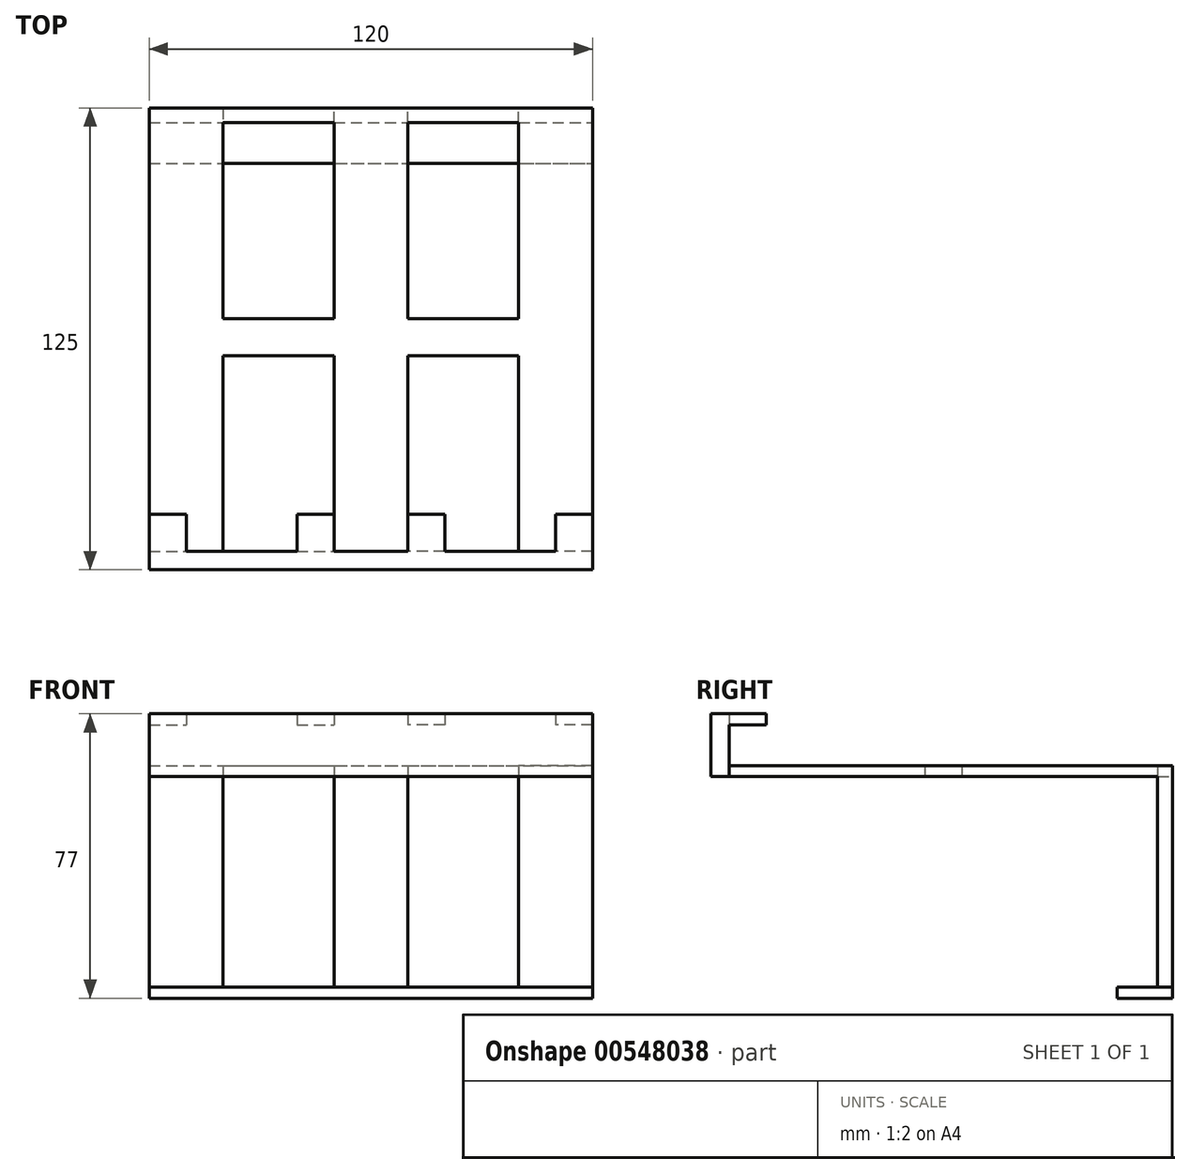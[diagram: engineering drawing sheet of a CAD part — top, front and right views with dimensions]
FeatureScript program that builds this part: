
annotation { "Feature Type Name" : "Feature", "Feature Type Description" : "" }
export const myFeature = defineFeature(function(context is Context, id is Id, definition is map)
    precondition{}
    {
        {
            var Q0;
            Q0=qCreatedBy(makeId("Top.planeOp"),FACE);
            var sketch = newSketch(context, id + "F0", { "sketchPlane" : qUnion([Q0])});
            skLineSegment(sketch, "E0.bottom", {"start": v(-56.42, -42.97) * mm, "end": v(63.58, -42.97) * mm});
            skLineSegment(sketch, "E0.top", {"start": v(-56.42, -47.97) * mm, "end": v(63.58, -47.97) * mm});
            skLineSegment(sketch, "E0.left", {"start": v(-56.42, -42.97) * mm, "end": v(-56.42, -47.97) * mm});
            skLineSegment(sketch, "E0.right", {"start": v(63.58, -42.97) * mm, "end": v(63.58, -47.97) * mm});
            skSolve(sketch);
        }
        {
            var Q0;
            Q0=makeQuery(id+"F0.imprint","IMPRINT",FACE,{"disambiguationData":[TD([[makeQuery(id+"F0.imprint","IMPRINT",EDGE,{"derivedFrom":sQuery(id+"F0.wireOp",EDGE,"E0.bottom")}),-1.0]])]});
            extrude(context, id + "F1", {"entities" : qUnion([Q0]), "depth" : 17 * mm, "offsetDistance" : 25 * mm});
        }
        {
            var Q0;
            Q0=makeQuery(id+"F1.opExtrude","SWEPT_FACE",FACE,{"disambiguationData":[OSD([sQuery(id+"F0.wireOp",EDGE,"E0.bottom")])]});
            var sketch = newSketch(context, id + "F2", { "sketchPlane" : qUnion([Q0])});
            skLineSegment(sketch, "E1.bottom", {"start": v(56.42, 17) * mm, "end": v(46.42, 17) * mm});
            skLineSegment(sketch, "E1.top", {"start": v(56.42, 14) * mm, "end": v(46.42, 14) * mm});
            skLineSegment(sketch, "E1.left", {"start": v(56.42, 17) * mm, "end": v(56.42, 14) * mm});
            skLineSegment(sketch, "E1.right", {"start": v(46.42, 17) * mm, "end": v(46.42, 14) * mm});
            skLineSegment(sketch, "E2.bottom", {"start": v(-63.58, 17) * mm, "end": v(-53.58, 17) * mm});
            skLineSegment(sketch, "E2.top", {"start": v(-63.58, 14) * mm, "end": v(-53.58, 14) * mm});
            skLineSegment(sketch, "E2.left", {"start": v(-63.58, 17) * mm, "end": v(-63.58, 14) * mm});
            skLineSegment(sketch, "E2.right", {"start": v(-53.58, 17) * mm, "end": v(-53.58, 14) * mm});
            skLineSegment(sketch, "E3.bottom", {"start": v(16.42, 17) * mm, "end": v(6.42, 17) * mm});
            skLineSegment(sketch, "E3.top", {"start": v(16.42, 14) * mm, "end": v(6.42, 14) * mm});
            skLineSegment(sketch, "E3.left", {"start": v(16.42, 17) * mm, "end": v(16.42, 14) * mm});
            skLineSegment(sketch, "E3.right", {"start": v(6.42, 17) * mm, "end": v(6.42, 14) * mm});
            skLineSegment(sketch, "E4.bottom", {"start": v(-23.58, 17) * mm, "end": v(-13.58, 17) * mm});
            skLineSegment(sketch, "E4.top", {"start": v(-23.58, 14) * mm, "end": v(-13.58, 14) * mm});
            skLineSegment(sketch, "E4.left", {"start": v(-23.58, 17) * mm, "end": v(-23.58, 14) * mm});
            skLineSegment(sketch, "E4.right", {"start": v(-13.58, 17) * mm, "end": v(-13.58, 14) * mm});
            skSolve(sketch);
        }
        {
            var Q0;
            Q0 = qSketchRegion(id + "F2", true);
            extrude(context, id + "F3", {"entities" : qUnion([Q0]), "operationType" : NewBodyOperationType.ADD, "depth" : 10 * mm, "offsetDistance" : 25 * mm});
        }
        {
            var Q0;
            Q0=makeQuery(id+"F1.opExtrude","SWEPT_FACE",FACE,{"disambiguationData":[OSD([sQuery(id+"F0.wireOp",EDGE,"E0.bottom")])]});
            var sketch = newSketch(context, id + "F4", { "sketchPlane" : qUnion([Q0])});
            skLineSegment(sketch, "E5.bottom", {"start": v(56.42, 0) * mm, "end": v(36.42, 0) * mm});
            skLineSegment(sketch, "E5.top", {"start": v(56.42, 3) * mm, "end": v(36.42, 3) * mm});
            skLineSegment(sketch, "E5.left", {"start": v(56.42, 0) * mm, "end": v(56.42, 3) * mm});
            skLineSegment(sketch, "E5.right", {"start": v(36.42, 0) * mm, "end": v(36.42, 3) * mm});
            skLineSegment(sketch, "E6.bottom", {"start": v(-63.58, 0) * mm, "end": v(-43.58, 0) * mm});
            skLineSegment(sketch, "E6.top", {"start": v(-63.58, 3) * mm, "end": v(-43.58, 3) * mm});
            skLineSegment(sketch, "E6.left", {"start": v(-63.58, 0) * mm, "end": v(-63.58, 3) * mm});
            skLineSegment(sketch, "E6.right", {"start": v(-43.58, 0) * mm, "end": v(-43.58, 3) * mm});
            skLineSegment(sketch, "E7.bottom", {"start": v(6.42, 0) * mm, "end": v(-13.58, 0) * mm});
            skLineSegment(sketch, "E7.top", {"start": v(6.42, 3) * mm, "end": v(-13.58, 3) * mm});
            skLineSegment(sketch, "E7.left", {"start": v(6.42, 0) * mm, "end": v(6.42, 3) * mm});
            skLineSegment(sketch, "E7.right", {"start": v(-13.58, 0) * mm, "end": v(-13.58, 3) * mm});
            skPoint(sketch, "E8", {"position": v(-3.58, 0) * mm});
            skSolve(sketch);
        }
        {
            var Q0;
            Q0=makeQuery(id+"F4.imprint","IMPRINT",FACE,{"disambiguationData":[TD([[makeQuery(id+"F4.imprint","IMPRINT",EDGE,{"derivedFrom":sQuery(id+"F4.wireOp",EDGE,"E5.bottom")}),-1.0]])]});
            var Q1;
            Q1=makeQuery(id+"F4.imprint","IMPRINT",FACE,{"disambiguationData":[TD([[makeQuery(id+"F4.imprint","IMPRINT",EDGE,{"derivedFrom":sQuery(id+"F4.wireOp",EDGE,"E7.bottom")}),-1.0]])]});
            var Q2;
            Q2=makeQuery(id+"F4.imprint","IMPRINT",FACE,{"disambiguationData":[TD([[makeQuery(id+"F4.imprint","IMPRINT",EDGE,{"derivedFrom":sQuery(id+"F4.wireOp",EDGE,"E6.bottom")}),-1.0]])]});
            extrude(context, id + "F5", {"entities" : qUnion([Q0, Q1, Q2]), "depth" : 120 * mm, "offsetDistance" : 25 * mm});
        }
        {
            var Q0;
            Q0=makeQuery(id+"F5.boolean.opBoolean","MERGE",FACE,{"derivedFrom":[makeQuery(id+"F1.opExtrude","CAP_FACE",FACE,{"disambiguationData":[OSD([sQuery(id+"F0.wireOp",EDGE,"E0.bottom"),sQuery(id+"F0.wireOp",EDGE,"E0.top"),sQuery(id+"F0.wireOp",EDGE,"E0.left"),sQuery(id+"F0.wireOp",EDGE,"E0.right")])],"isStart":true}),makeQuery(id+"F5.opExtrude","SWEPT_FACE",FACE,{"disambiguationData":[OSD([sQuery(id+"F4.wireOp",EDGE,"E5.bottom")])]}),makeQuery(id+"F5.opExtrude","SWEPT_FACE",FACE,{"disambiguationData":[OSD([sQuery(id+"F4.wireOp",EDGE,"E6.bottom")])]}),makeQuery(id+"F5.opExtrude","SWEPT_FACE",FACE,{"disambiguationData":[OSD([sQuery(id+"F4.wireOp",EDGE,"E7.bottom")])]})]});
            var sketch = newSketch(context, id + "F6", { "sketchPlane" : qUnion([Q0])});
            skLineSegment(sketch, "E9.bottom", {"start": v(63.58, -77.03) * mm, "end": v(-56.42, -77.03) * mm});
            skLineSegment(sketch, "E9.top", {"start": v(63.58, -73.03) * mm, "end": v(-56.42, -73.03) * mm});
            skLineSegment(sketch, "E9.left", {"start": v(63.58, -77.03) * mm, "end": v(63.58, -73.03) * mm});
            skLineSegment(sketch, "E9.right", {"start": v(-56.42, -77.03) * mm, "end": v(-56.42, -73.03) * mm});
            skSolve(sketch);
        }
        {
            var Q0;
            Q0 = qSketchRegion(id + "F6", true);
            extrude(context, id + "F7", {"entities" : qUnion([Q0]), "operationType" : NewBodyOperationType.ADD, "oppositeDirection" : true, "depth" : 3 * mm, "offsetDistance" : 25 * mm});
        }
        {
            var Q0;
            Q0=makeQuery(id+"F7.boolean.opBoolean","MERGE",FACE,{"derivedFrom":[makeQuery(id+"F5.boolean.opBoolean","MERGE",FACE,{"derivedFrom":[makeQuery(id+"F1.opExtrude","CAP_FACE",FACE,{"disambiguationData":[OSD([sQuery(id+"F0.wireOp",EDGE,"E0.bottom"),sQuery(id+"F0.wireOp",EDGE,"E0.top"),sQuery(id+"F0.wireOp",EDGE,"E0.left"),sQuery(id+"F0.wireOp",EDGE,"E0.right")])],"isStart":true}),makeQuery(id+"F5.opExtrude","SWEPT_FACE",FACE,{"disambiguationData":[OSD([sQuery(id+"F4.wireOp",EDGE,"E5.bottom")])]}),makeQuery(id+"F5.opExtrude","SWEPT_FACE",FACE,{"disambiguationData":[OSD([sQuery(id+"F4.wireOp",EDGE,"E6.bottom")])]}),makeQuery(id+"F5.opExtrude","SWEPT_FACE",FACE,{"disambiguationData":[OSD([sQuery(id+"F4.wireOp",EDGE,"E7.bottom")])]})]}),makeQuery(id+"F7.opExtrude","CAP_FACE",FACE,{"disambiguationData":[OSD([sQuery(id+"F6.wireOp",EDGE,"E9.bottom"),sQuery(id+"F6.wireOp",EDGE,"E9.top"),sQuery(id+"F6.wireOp",EDGE,"E9.left"),sQuery(id+"F6.wireOp",EDGE,"E9.right")])],"isStart":true})]});
            var sketch = newSketch(context, id + "F8", { "sketchPlane" : qUnion([Q0])});
            skLineSegment(sketch, "E10.bottom", {"start": v(-56.42, -77.03) * mm, "end": v(-36.42, -77.03) * mm});
            skLineSegment(sketch, "E10.top", {"start": v(-56.42, -73.03) * mm, "end": v(-36.42, -73.03) * mm});
            skLineSegment(sketch, "E10.left", {"start": v(-56.42, -77.03) * mm, "end": v(-56.42, -73.03) * mm});
            skLineSegment(sketch, "E10.right", {"start": v(-36.42, -77.03) * mm, "end": v(-36.42, -73.03) * mm});
            skLineSegment(sketch, "E11.bottom", {"start": v(-6.42, -73.03) * mm, "end": v(13.58, -73.03) * mm});
            skLineSegment(sketch, "E11.top", {"start": v(-6.42, -77.03) * mm, "end": v(13.58, -77.03) * mm});
            skLineSegment(sketch, "E11.left", {"start": v(-6.42, -73.03) * mm, "end": v(-6.42, -77.03) * mm});
            skLineSegment(sketch, "E11.right", {"start": v(13.58, -73.03) * mm, "end": v(13.58, -77.03) * mm});
            skLineSegment(sketch, "E12.bottom", {"start": v(43.58, -73.03) * mm, "end": v(63.58, -73.03) * mm});
            skLineSegment(sketch, "E12.top", {"start": v(43.58, -77.03) * mm, "end": v(63.58, -77.03) * mm});
            skLineSegment(sketch, "E12.left", {"start": v(43.58, -73.03) * mm, "end": v(43.58, -77.03) * mm});
            skLineSegment(sketch, "E12.right", {"start": v(63.58, -73.03) * mm, "end": v(63.58, -77.03) * mm});
            skSolve(sketch);
        }
        {
            var Q0;
            Q0=makeQuery(id+"F8.imprint","IMPRINT",FACE,{"disambiguationData":[TD([[makeQuery(id+"F8.imprint","IMPRINT",EDGE,{"derivedFrom":sQuery(id+"F8.wireOp",EDGE,"E10.bottom")}),1.0]])]});
            var Q1;
            Q1=makeQuery(id+"F8.imprint","IMPRINT",FACE,{"disambiguationData":[TD([[makeQuery(id+"F8.imprint","IMPRINT",EDGE,{"derivedFrom":sQuery(id+"F8.wireOp",EDGE,"E11.bottom")}),-1.0]])]});
            var Q2;
            Q2=makeQuery(id+"F8.imprint","IMPRINT",FACE,{"disambiguationData":[TD([[makeQuery(id+"F8.imprint","IMPRINT",EDGE,{"derivedFrom":sQuery(id+"F8.wireOp",EDGE,"E12.bottom")}),-1.0]])]});
            extrude(context, id + "F9", {"entities" : qUnion([Q0, Q1, Q2]), "operationType" : NewBodyOperationType.ADD, "depth" : 57 * mm, "offsetDistance" : 25 * mm});
        }
        {
            var Q0;
            Q0=makeQuery(id+"F9.boolean.opBoolean","MERGE",FACE,{"derivedFrom":[makeQuery(id+"F7.boolean.opBoolean","MERGE",FACE,{"derivedFrom":[makeQuery(id+"F5.opExtrude","CAP_FACE",FACE,{"disambiguationData":[OSD([sQuery(id+"F4.wireOp",EDGE,"E5.bottom"),sQuery(id+"F4.wireOp",EDGE,"E5.top"),sQuery(id+"F4.wireOp",EDGE,"E5.left"),sQuery(id+"F4.wireOp",EDGE,"E5.right")])],"isStart":false}),makeQuery(id+"F5.opExtrude","CAP_FACE",FACE,{"disambiguationData":[OSD([sQuery(id+"F4.wireOp",EDGE,"E6.bottom"),sQuery(id+"F4.wireOp",EDGE,"E6.top"),sQuery(id+"F4.wireOp",EDGE,"E6.left"),sQuery(id+"F4.wireOp",EDGE,"E6.right")])],"isStart":false}),makeQuery(id+"F5.opExtrude","CAP_FACE",FACE,{"disambiguationData":[OSD([sQuery(id+"F4.wireOp",EDGE,"E7.bottom"),sQuery(id+"F4.wireOp",EDGE,"E7.top"),sQuery(id+"F4.wireOp",EDGE,"E7.left"),sQuery(id+"F4.wireOp",EDGE,"E7.right")])],"isStart":false}),makeQuery(id+"F7.opExtrude","SWEPT_FACE",FACE,{"disambiguationData":[OSD([sQuery(id+"F6.wireOp",EDGE,"E9.bottom")])]})]}),makeQuery(id+"F9.opExtrude","SWEPT_FACE",FACE,{"disambiguationData":[OSD([sQuery(id+"F8.wireOp",EDGE,"E10.bottom")])]}),makeQuery(id+"F9.opExtrude","SWEPT_FACE",FACE,{"disambiguationData":[OSD([sQuery(id+"F8.wireOp",EDGE,"E11.top")])]}),makeQuery(id+"F9.opExtrude","SWEPT_FACE",FACE,{"disambiguationData":[OSD([sQuery(id+"F8.wireOp",EDGE,"E12.top")])]})]});
            var sketch = newSketch(context, id + "F10", { "sketchPlane" : qUnion([Q0])});
            skLineSegment(sketch, "E13.bottom", {"start": v(56.42, -57) * mm, "end": v(-63.58, -57) * mm});
            skLineSegment(sketch, "E13.top", {"start": v(56.42, -60) * mm, "end": v(-63.58, -60) * mm});
            skLineSegment(sketch, "E13.left", {"start": v(56.42, -57) * mm, "end": v(56.42, -60) * mm});
            skLineSegment(sketch, "E13.right", {"start": v(-63.58, -57) * mm, "end": v(-63.58, -60) * mm});
            skSolve(sketch);
        }
        {
            var Q0;
            Q0=makeQuery(id+"F10.imprint","IMPRINT",FACE,{"disambiguationData":[TD([[makeQuery(id+"F10.imprint","IMPRINT",EDGE,{"derivedFrom":sQuery(id+"F10.wireOp",EDGE,"E13.top")}),-1.0]])]});
            extrude(context, id + "F11", {"entities" : qUnion([Q0]), "oppositeDirection" : true, "depth" : 15 * mm, "offsetDistance" : 25 * mm});
        }
        {
            var Q0;
            Q0=makeQuery(id+"F5.opExtrude","SWEPT_FACE",FACE,{"disambiguationData":[OSD([sQuery(id+"F4.wireOp",EDGE,"E6.right")])]});
            var sketch = newSketch(context, id + "F12", { "sketchPlane" : qUnion([Q0])});
            skLineSegment(sketch, "E14.bottom", {"start": v(-20.03, 3) * mm, "end": v(-10.03, 3) * mm});
            skLineSegment(sketch, "E14.top", {"start": v(-20.03, 0) * mm, "end": v(-10.03, 0) * mm});
            skLineSegment(sketch, "E14.left", {"start": v(-20.03, 3) * mm, "end": v(-20.03, 0) * mm});
            skLineSegment(sketch, "E14.right", {"start": v(-10.03, 3) * mm, "end": v(-10.03, 0) * mm});
            skPoint(sketch, "E15", {"position": v(-15.03, 3) * mm});
            skSolve(sketch);
        }
        {
            var Q0;
            Q0 = qSketchRegion(id + "F12", true);
            extrude(context, id + "F13", {"entities" : qUnion([Q0]), "operationType" : NewBodyOperationType.ADD, "depth" : 85 * mm, "offsetDistance" : 25 * mm});
        }
    });
